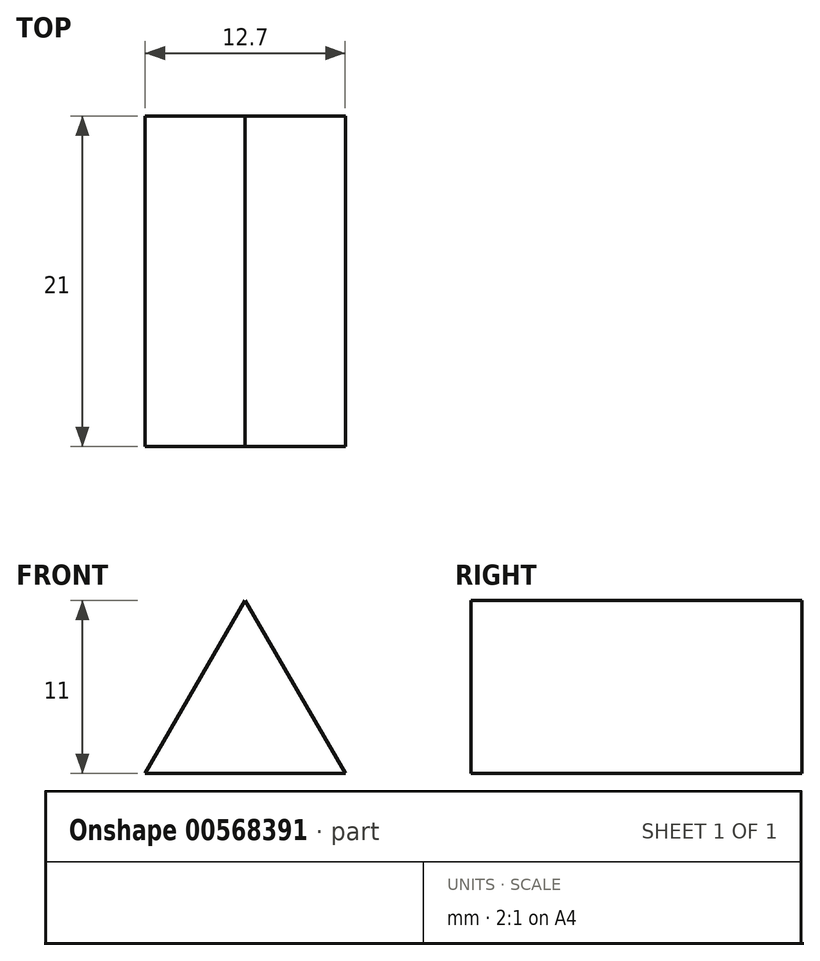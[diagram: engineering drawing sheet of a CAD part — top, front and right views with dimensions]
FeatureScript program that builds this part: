
annotation { "Feature Type Name" : "Feature", "Feature Type Description" : "" }
export const myFeature = defineFeature(function(context is Context, id is Id, definition is map)
    precondition{}
    {
        {
            var Q0;
            Q0=qCreatedBy(makeId("Front.planeOp"),FACE);
            var sketch = newSketch(context, id + "F0", { "sketchPlane" : qUnion([Q0])});
            skLineSegment(sketch, "E0", {"start": v(-6.35, 0) * mm, "end": v(6.35, 0) * mm});
            skLineSegment(sketch, "E1", {"start": v(6.35, 0) * mm, "end": v(0, 11) * mm});
            skLineSegment(sketch, "E2", {"start": v(0, 11) * mm, "end": v(-6.35, 0) * mm});
            skSolve(sketch);
        }
        {
            var Q0;
            Q0 = qSketchRegion(id + "F0", true);
            extrude(context, id + "F1", {"entities" : qUnion([Q0]), "depth" : 21 * mm, "offsetDistance" : 25 * mm});
        }
    });
